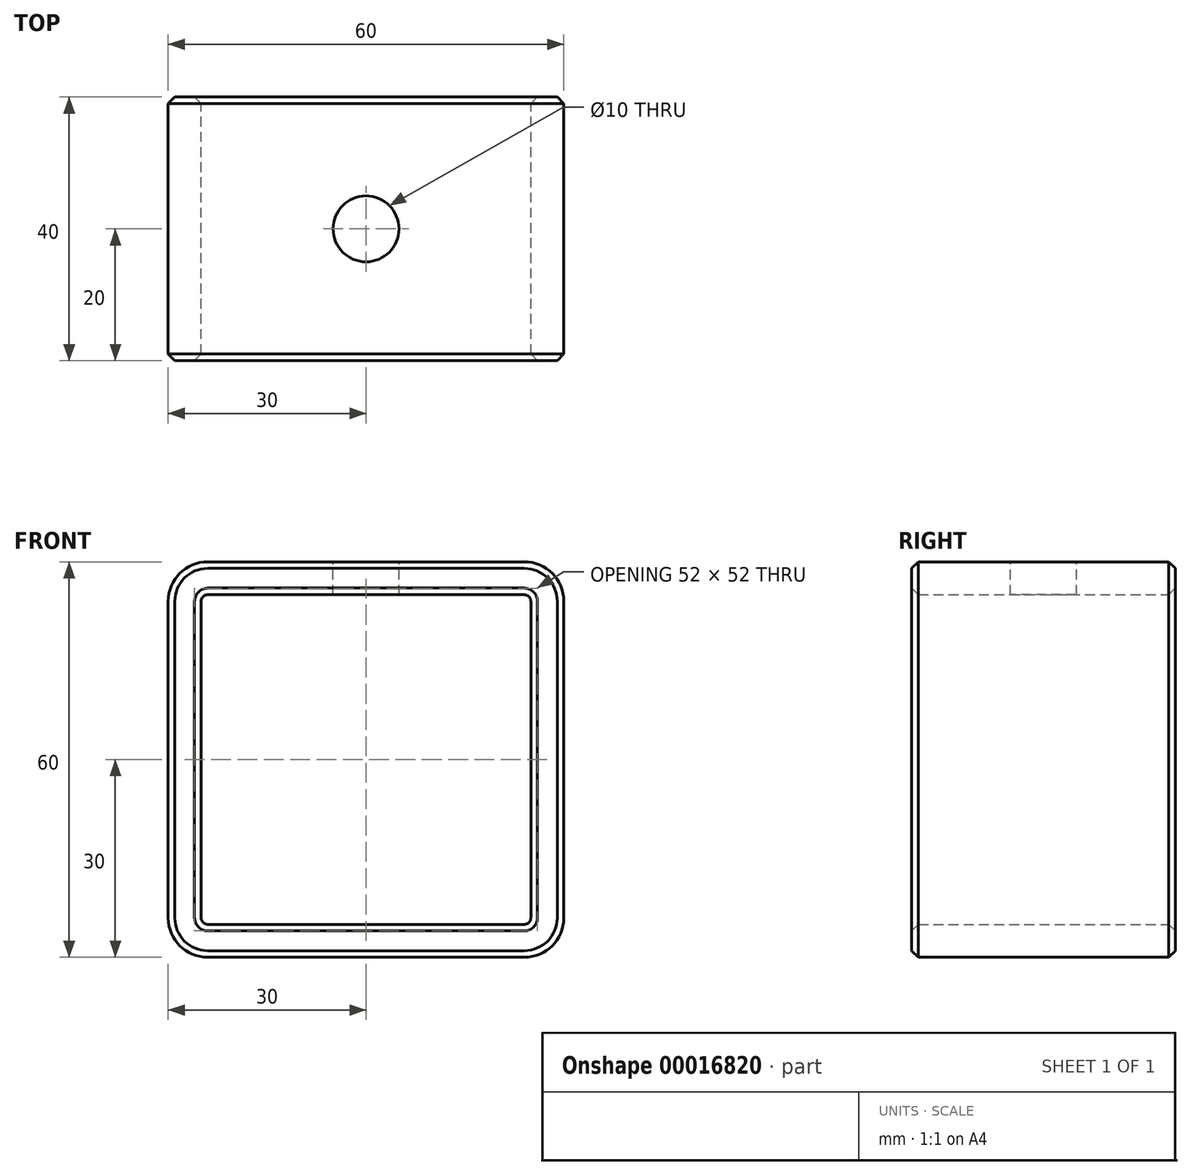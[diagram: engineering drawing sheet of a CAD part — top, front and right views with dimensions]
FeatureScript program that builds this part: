
annotation { "Feature Type Name" : "Feature", "Feature Type Description" : "" }
export const myFeature = defineFeature(function(context is Context, id is Id, definition is map)
    precondition{}
    {
        {
            var Q0;
            Q0=qCreatedBy(makeId("Front.planeOp"),FACE);
            var sketch = newSketch(context, id + "F0", { "sketchPlane" : qUnion([Q0])});
            skLineSegment(sketch, "E0.bottom", {"start": v(6, 0) * mm, "end": v(54, 0) * mm});
            skLineSegment(sketch, "E0.top", {"start": v(6, 60) * mm, "end": v(54, 60) * mm});
            skLineSegment(sketch, "E0.left", {"start": v(0, 6) * mm, "end": v(0, 54) * mm});
            skLineSegment(sketch, "E0.right", {"start": v(60, 6) * mm, "end": v(60, 54) * mm});
            skPoint(sketch, "E1.visualSharp", {"position": v(0, 0) * mm});
            skArc(sketch, "E1.filletArc", {"start": v(0, 6) * mm, "mid": v(1.76, 1.76) * mm, "end": v(6, 0) * mm});
            skPoint(sketch, "E2.visualSharp", {"position": v(0, 60) * mm});
            skArc(sketch, "E2.filletArc", {"start": v(6, 60) * mm, "mid": v(1.76, 58.24) * mm, "end": v(0, 54) * mm});
            skPoint(sketch, "E3.visualSharp", {"position": v(60, 60) * mm});
            skArc(sketch, "E3.filletArc", {"start": v(60, 54) * mm, "mid": v(58.24, 58.24) * mm, "end": v(54, 60) * mm});
            skPoint(sketch, "E4.visualSharp", {"position": v(60, 0) * mm});
            skArc(sketch, "E4.filletArc", {"start": v(54, 0) * mm, "mid": v(58.24, 1.76) * mm, "end": v(60, 6) * mm});
            skLineSegment(sketch, "E5.0", {"start": v(6, 55) * mm, "end": v(54, 55) * mm});
            skLineSegment(sketch, "E6.0", {"start": v(5, 6) * mm, "end": v(5, 54) * mm});
            skLineSegment(sketch, "E7.0", {"start": v(6, 5) * mm, "end": v(54, 5) * mm});
            skLineSegment(sketch, "E8.0", {"start": v(55, 6) * mm, "end": v(55, 54) * mm});
            skArc(sketch, "E9.0", {"start": v(54, 5) * mm, "mid": v(54.7, 5.3) * mm, "end": v(55, 6) * mm});
            skArc(sketch, "E10.0", {"start": v(55, 54) * mm, "mid": v(54.7, 54.7) * mm, "end": v(54, 55) * mm});
            skArc(sketch, "E11.0", {"start": v(6, 55) * mm, "mid": v(5.3, 54.7) * mm, "end": v(5, 54) * mm});
            skArc(sketch, "E12.0", {"start": v(5, 6) * mm, "mid": v(5.3, 5.3) * mm, "end": v(6, 5) * mm});
            skSolve(sketch);
        }
        {
            var Q0;
            Q0=makeQuery(id+"F0.imprint","IMPRINT",FACE,{"disambiguationData":[TD([[makeQuery(id+"F0.imprint","IMPRINT",EDGE,{"derivedFrom":sQuery(id+"F0.wireOp",EDGE,"E0.bottom")}),1.0]])]});
            extrude(context, id + "F1", {"entities" : qUnion([Q0]), "depth" : 40 * mm});
        }
        {
            var Q0;
            Q0=makeQuery(id+"F1.opExtrude","SWEPT_FACE",FACE,{"disambiguationData":[OSD([sQuery(id+"F0.wireOp",EDGE,"E0.top")])]});
            var sketch = newSketch(context, id + "F2", { "sketchPlane" : qUnion([Q0])});
            skLineSegment(sketch, "E13", {"start": v(6, 0) * mm, "end": v(54, -40) * mm, "construction": true});
            skLineSegment(sketch, "E14", {"start": v(6, -40) * mm, "end": v(54, 0) * mm, "construction": true});
            skCircle(sketch, "E15", {"center": v(30, -20) * mm, "radius": 5 * mm});
            skSolve(sketch);
        }
        {
            var Q0;
            Q0=makeQuery(id+"F2.imprint","IMPRINT",FACE,{"disambiguationData":[TD([[makeQuery(id+"F2.imprint","IMPRINT",EDGE,{"derivedFrom":sQuery(id+"F2.wireOp",EDGE,"E15")}),1.0]])]});
            var Q1;
            Q1=sQuery(id+"F2.wireOp",EDGE,"E13");
            var Q2;
            Q2=sQuery(id+"F2.wireOp",EDGE,"E14");
            var Q3;
            Q3=sQuery(id+"F2.wireOp",EDGE,"E15");
            extrude(context, id + "F3", {"entities" : qUnion([Q0]), "operationType" : NewBodyOperationType.REMOVE, "surfaceEntities" : qUnion([Q1, Q2, Q3]), "oppositeDirection" : true, "depth" : 25 * mm});
        }
        {
            var Q0;
            Q0=makeQuery(id+"F1.opExtrude","CAP_EDGE",EDGE,{"disambiguationData":[OSD([sQuery(id+"F0.wireOp",EDGE,"E0.top")])],"isStart":false});
            var Q1;
            Q1=makeQuery(id+"F1.opExtrude","CAP_EDGE",EDGE,{"disambiguationData":[OSD([sQuery(id+"F0.wireOp",EDGE,"E2.filletArc")])],"isStart":false});
            var Q2;
            Q2=makeQuery(id+"F1.opExtrude","CAP_FACE",FACE,{"disambiguationData":[OSD([sQuery(id+"F0.wireOp",EDGE,"E0.bottom"),sQuery(id+"F0.wireOp",EDGE,"E0.top"),sQuery(id+"F0.wireOp",EDGE,"E0.left"),sQuery(id+"F0.wireOp",EDGE,"E0.right"),sQuery(id+"F0.wireOp",EDGE,"E1.filletArc"),sQuery(id+"F0.wireOp",EDGE,"E2.filletArc"),sQuery(id+"F0.wireOp",EDGE,"E3.filletArc"),sQuery(id+"F0.wireOp",EDGE,"E4.filletArc"),sQuery(id+"F0.wireOp",EDGE,"E5.0"),sQuery(id+"F0.wireOp",EDGE,"E6.0"),sQuery(id+"F0.wireOp",EDGE,"E7.0"),sQuery(id+"F0.wireOp",EDGE,"E8.0"),sQuery(id+"F0.wireOp",EDGE,"E9.0"),sQuery(id+"F0.wireOp",EDGE,"E10.0"),sQuery(id+"F0.wireOp",EDGE,"E11.0"),sQuery(id+"F0.wireOp",EDGE,"E12.0")])],"isStart":false});
            chamfer(context, id + "F4", {"entities" : qUnion([Q0, Q1, Q2]), "width" : 1 * mm, "tangentPropagation" : true});
        }
        {
            var Q0;
            Q0=makeQuery(id+"F1.opExtrude","CAP_FACE",FACE,{"disambiguationData":[OSD([sQuery(id+"F0.wireOp",EDGE,"E0.bottom"),sQuery(id+"F0.wireOp",EDGE,"E0.top"),sQuery(id+"F0.wireOp",EDGE,"E0.left"),sQuery(id+"F0.wireOp",EDGE,"E0.right"),sQuery(id+"F0.wireOp",EDGE,"E1.filletArc"),sQuery(id+"F0.wireOp",EDGE,"E2.filletArc"),sQuery(id+"F0.wireOp",EDGE,"E3.filletArc"),sQuery(id+"F0.wireOp",EDGE,"E4.filletArc"),sQuery(id+"F0.wireOp",EDGE,"E5.0"),sQuery(id+"F0.wireOp",EDGE,"E6.0"),sQuery(id+"F0.wireOp",EDGE,"E7.0"),sQuery(id+"F0.wireOp",EDGE,"E8.0"),sQuery(id+"F0.wireOp",EDGE,"E9.0"),sQuery(id+"F0.wireOp",EDGE,"E10.0"),sQuery(id+"F0.wireOp",EDGE,"E11.0"),sQuery(id+"F0.wireOp",EDGE,"E12.0")])],"isStart":true});
            chamfer(context, id + "F5", {"entities" : qUnion([Q0]), "width" : 1 * mm, "tangentPropagation" : true});
        }
    });
